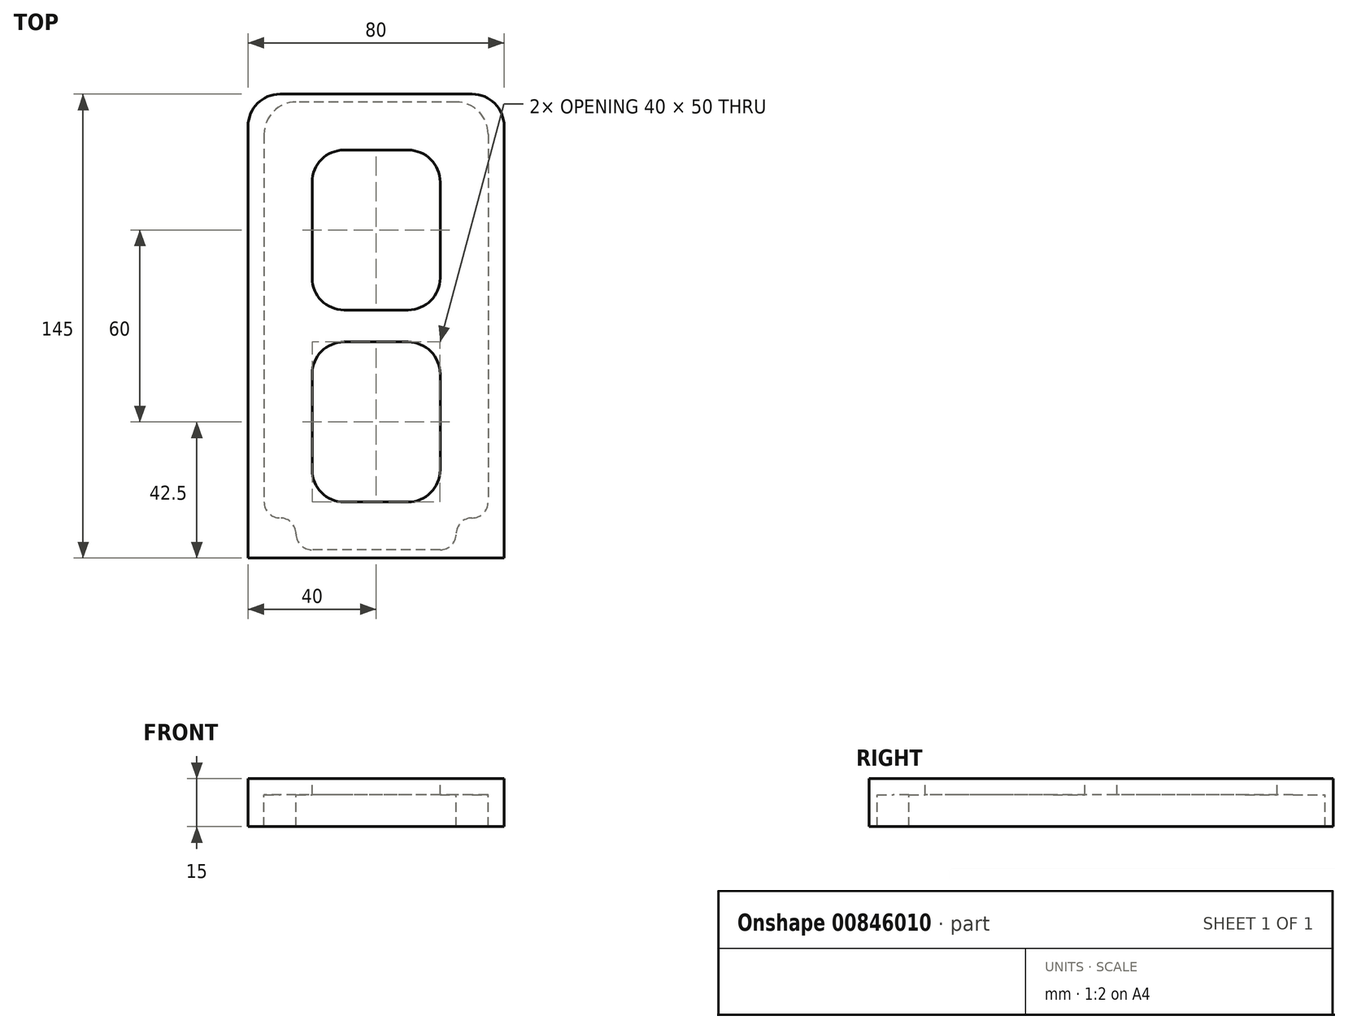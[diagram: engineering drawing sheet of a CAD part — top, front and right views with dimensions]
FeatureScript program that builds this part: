
annotation { "Feature Type Name" : "Feature", "Feature Type Description" : "" }
export const myFeature = defineFeature(function(context is Context, id is Id, definition is map)
    precondition{}
    {
        {
            var Q0;
            Q0=qCreatedBy(makeId("Top.planeOp"),FACE);
            var sketch = newSketch(context, id + "F0", { "sketchPlane" : qUnion([Q0])});
            skLineSegment(sketch, "E0.bottom", {"start": v(30, 72.5) * mm, "end": v(-30, 72.5) * mm});
            skLineSegment(sketch, "E0.top", {"start": v(40, -72.5) * mm, "end": v(-40, -72.5) * mm});
            skLineSegment(sketch, "E0.left", {"start": v(40, 62.5) * mm, "end": v(40, -72.5) * mm});
            skLineSegment(sketch, "E0.right", {"start": v(-40, 62.5) * mm, "end": v(-40, -72.5) * mm});
            skPoint(sketch, "E0.middle", {"position": v(0, 0) * mm});
            skLineSegment(sketch, "E1.bottom", {"start": v(25, 70) * mm, "end": v(-25, 70) * mm});
            skLineSegment(sketch, "E1.top", {"start": v(20, -70) * mm, "end": v(-20, -70) * mm});
            skLineSegment(sketch, "E1.left", {"start": v(35, 60) * mm, "end": v(35, -55) * mm});
            skLineSegment(sketch, "E1.right", {"start": v(-35, 60) * mm, "end": v(-35, -55) * mm});
            skPoint(sketch, "E2.visualSharp", {"position": v(-35, 70) * mm});
            skArc(sketch, "E2.filletArc", {"start": v(-25, 70) * mm, "mid": v(-32.07, 67.07) * mm, "end": v(-35, 60) * mm});
            skPoint(sketch, "E3.visualSharp", {"position": v(-40, 72.5) * mm});
            skArc(sketch, "E3.filletArc", {"start": v(-30, 72.5) * mm, "mid": v(-37.07, 69.57) * mm, "end": v(-40, 62.5) * mm});
            skPoint(sketch, "E4.visualSharp", {"position": v(35, 70) * mm});
            skArc(sketch, "E4.filletArc", {"start": v(35, 60) * mm, "mid": v(32.07, 67.07) * mm, "end": v(25, 70) * mm});
            skPoint(sketch, "E5.visualSharp", {"position": v(40, 72.5) * mm});
            skArc(sketch, "E5.filletArc", {"start": v(40, 62.5) * mm, "mid": v(37.07, 69.57) * mm, "end": v(30, 72.5) * mm});
            skLineSegment(sketch, "E6.bottom", {"start": v(10, 55) * mm, "end": v(-10, 55) * mm});
            skLineSegment(sketch, "E6.top", {"start": v(10, -55) * mm, "end": v(-10, -55) * mm});
            skPoint(sketch, "E7.visualSharp", {"position": v(-20, 55) * mm});
            skArc(sketch, "E7.filletArc", {"start": v(-10, 55) * mm, "mid": v(-17.07, 52.07) * mm, "end": v(-20, 45) * mm});
            skPoint(sketch, "E8.visualSharp", {"position": v(20, 55) * mm});
            skArc(sketch, "E8.filletArc", {"start": v(20, 45) * mm, "mid": v(17.07, 52.07) * mm, "end": v(10, 55) * mm});
            skPoint(sketch, "E9.visualSharp", {"position": v(-20, -55) * mm});
            skArc(sketch, "E9.filletArc", {"start": v(-20, -45) * mm, "mid": v(-17.07, -52.07) * mm, "end": v(-10, -55) * mm});
            skPoint(sketch, "E10.visualSharp", {"position": v(20, -55) * mm});
            skArc(sketch, "E10.filletArc", {"start": v(10, -55) * mm, "mid": v(17.07, -52.07) * mm, "end": v(20, -45) * mm});
            skLineSegment(sketch, "E11", {"start": v(-20, -15) * mm, "end": v(-20, -45) * mm});
            skLineSegment(sketch, "E12", {"start": v(-10, -5) * mm, "end": v(10, -5) * mm});
            skLineSegment(sketch, "E13", {"start": v(20, -15) * mm, "end": v(20, -45) * mm});
            skLineSegment(sketch, "E14", {"start": v(-20, 45) * mm, "end": v(-20, 15) * mm});
            skLineSegment(sketch, "E15", {"start": v(-10, 5) * mm, "end": v(10, 5) * mm});
            skLineSegment(sketch, "E16", {"start": v(20, 15) * mm, "end": v(20, 45) * mm});
            skPoint(sketch, "E17.visualSharp", {"position": v(-20, -5) * mm});
            skArc(sketch, "E17.filletArc", {"start": v(-10, -5) * mm, "mid": v(-17.07, -7.93) * mm, "end": v(-20, -15) * mm});
            skPoint(sketch, "E18.visualSharp", {"position": v(20, -5) * mm});
            skArc(sketch, "E18.filletArc", {"start": v(20, -15) * mm, "mid": v(17.07, -7.93) * mm, "end": v(10, -5) * mm});
            skPoint(sketch, "E19.visualSharp", {"position": v(20, 5) * mm});
            skArc(sketch, "E19.filletArc", {"start": v(10, 5) * mm, "mid": v(17.07, 7.93) * mm, "end": v(20, 15) * mm});
            skPoint(sketch, "E20.visualSharp", {"position": v(-20, 5) * mm});
            skArc(sketch, "E20.filletArc", {"start": v(-20, 15) * mm, "mid": v(-17.07, 7.93) * mm, "end": v(-10, 5) * mm});
            skLineSegment(sketch, "E21", {"start": v(25, -65) * mm, "end": v(25, -65) * mm});
            skLineSegment(sketch, "E22", {"start": v(30, -60) * mm, "end": v(30, -60) * mm});
            skPoint(sketch, "E23.visualSharp", {"position": v(25, -60) * mm});
            skArc(sketch, "E23.filletArc", {"start": v(30, -60) * mm, "mid": v(26.46, -61.46) * mm, "end": v(25, -65) * mm});
            skPoint(sketch, "E24.visualSharp", {"position": v(25, -70) * mm});
            skArc(sketch, "E24.filletArc", {"start": v(20, -70) * mm, "mid": v(23.54, -68.54) * mm, "end": v(25, -65) * mm});
            skPoint(sketch, "E25.visualSharp", {"position": v(35, -60) * mm});
            skArc(sketch, "E25.filletArc", {"start": v(30, -60) * mm, "mid": v(33.54, -58.54) * mm, "end": v(35, -55) * mm});
            skLineSegment(sketch, "E26", {"start": v(-30, -60) * mm, "end": v(-30, -60) * mm});
            skLineSegment(sketch, "E27", {"start": v(-25, -65) * mm, "end": v(-25, -65) * mm});
            skPoint(sketch, "E28.visualSharp", {"position": v(-25, -70) * mm});
            skArc(sketch, "E28.filletArc", {"start": v(-25, -65) * mm, "mid": v(-23.54, -68.54) * mm, "end": v(-20, -70) * mm});
            skPoint(sketch, "E29.visualSharp", {"position": v(-25, -60) * mm});
            skArc(sketch, "E29.filletArc", {"start": v(-25, -65) * mm, "mid": v(-26.46, -61.46) * mm, "end": v(-30, -60) * mm});
            skPoint(sketch, "E30.visualSharp", {"position": v(-35, -60) * mm});
            skArc(sketch, "E30.filletArc", {"start": v(-35, -55) * mm, "mid": v(-33.54, -58.54) * mm, "end": v(-30, -60) * mm});
            skSolve(sketch);
        }
        {
            var Q0;
            Q0=makeQuery(id+"F0.imprint","IMPRINT",FACE,{"disambiguationData":[TD([[makeQuery(id+"F0.imprint","IMPRINT",EDGE,{"derivedFrom":sQuery(id+"F0.wireOp",EDGE,"E0.bottom")}),1.0]])]});
            var Q1;
            Q1=makeQuery(id+"F0.imprint","IMPRINT",FACE,{"disambiguationData":[TD([[makeQuery(id+"F0.imprint","IMPRINT",EDGE,{"derivedFrom":sQuery(id+"F0.wireOp",EDGE,"E1.bottom")}),1.0]])]});
            extrude(context, id + "F1", {"entities" : qUnion([Q0, Q1]), "oppositeDirection" : true, "depth" : 5 * mm, "offsetDistance" : 25 * mm});
        }
        {
            var Q0;
            Q0=makeQuery(id+"F0.imprint","IMPRINT",FACE,{"disambiguationData":[TD([[makeQuery(id+"F0.imprint","IMPRINT",EDGE,{"derivedFrom":sQuery(id+"F0.wireOp",EDGE,"E0.bottom")}),1.0]])]});
            extrude(context, id + "F2", {"entities" : qUnion([Q0]), "operationType" : NewBodyOperationType.ADD, "oppositeDirection" : true, "depth" : 15 * mm, "offsetDistance" : 25 * mm});
        }
    });
